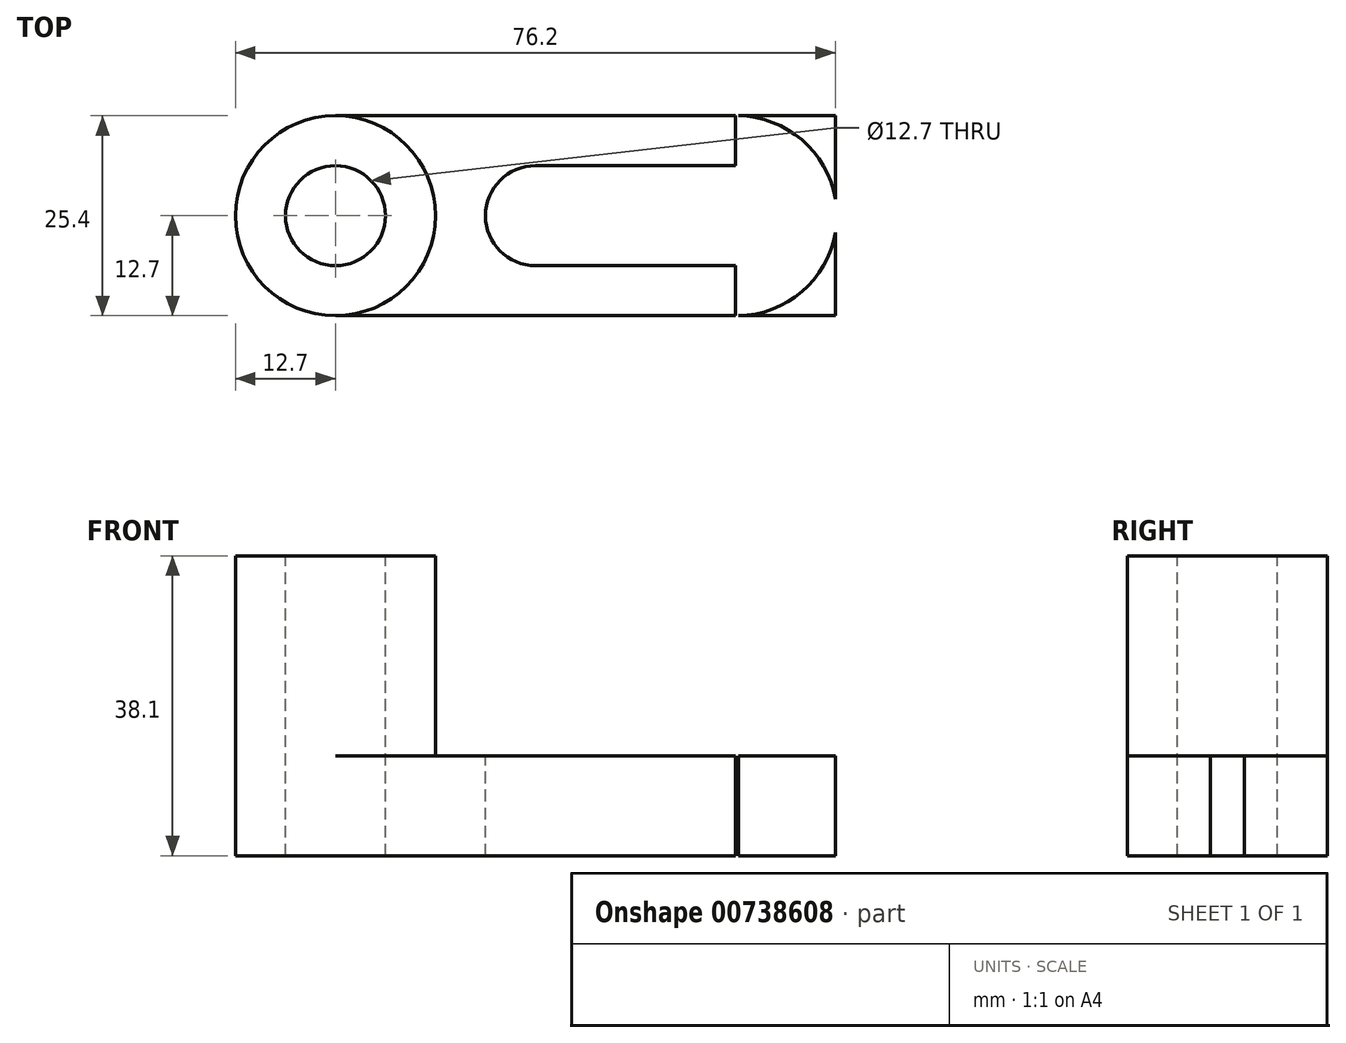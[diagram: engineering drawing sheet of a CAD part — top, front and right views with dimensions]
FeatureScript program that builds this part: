
annotation { "Feature Type Name" : "Feature", "Feature Type Description" : "" }
export const myFeature = defineFeature(function(context is Context, id is Id, definition is map)
    precondition{}
    {
        {
            var Q0;
            Q0=qCreatedBy(makeId("Front.planeOp"),FACE);
            var sketch = newSketch(context, id + "F0", { "sketchPlane" : qUnion([Q0])});
            skLineSegment(sketch, "E0", {"start": v(0, 38.1) * mm, "end": v(0, 0) * mm});
            skLineSegment(sketch, "E1", {"start": v(0, 0) * mm, "end": v(76.2, 0) * mm});
            skLineSegment(sketch, "E2", {"start": v(76.2, 0) * mm, "end": v(76.2, 12.7) * mm});
            skLineSegment(sketch, "E3", {"start": v(76.2, 12.7) * mm, "end": v(25.4, 12.7) * mm});
            skLineSegment(sketch, "E4", {"start": v(25.4, 12.7) * mm, "end": v(25.4, 38.1) * mm});
            skLineSegment(sketch, "E5", {"start": v(25.4, 38.1) * mm, "end": v(0, 38.1) * mm});
            skSolve(sketch);
        }
        {
            var Q0;
            Q0 = qSketchRegion(id + "F0", true);
            extrude(context, id + "F1", {"entities" : qUnion([Q0]), "depth" : 25.4 * mm, "offsetDistance" : 25.4 * mm});
        }
        {
            var Q0;
            Q0=makeQuery(id+"F1.opExtrude","SWEPT_FACE",FACE,{"disambiguationData":[OSD([sQuery(id+"F0.wireOp",EDGE,"E5")])]});
            var sketch = newSketch(context, id + "F2", { "sketchPlane" : qUnion([Q0])});
            skLineSegment(sketch, "E6", {"start": v(0, -12.7) * mm, "end": v(25.4, -12.7) * mm});
            skCircle(sketch, "E7", {"center": v(12.7, -12.7) * mm, "radius": 12.7 * mm});
            skCircle(sketch, "E8", {"center": v(12.7, -12.7) * mm, "radius": 6.35 * mm});
            skSolve(sketch);
        }
        {
            var Q0;
            {var subQ0=sQuery(id+"F2.wireOp",EDGE,"E8");var subQ1=sQuery(id+"F2.wireOp",EDGE,"E6");var subQ2=makeQuery(id+"F2.imprint","INTERSECT",VERTEX,{"disambiguationData":[OD(0.0)],"derivedFrom":[subQ1,subQ0]});Q0=makeQuery(id+"F2.imprint","IMPRINT",FACE,{"disambiguationData":[TD([[makeQuery(id+"F2.imprint","IMPRINT",EDGE,{"disambiguationData":[TD([[subQ2,-1.0]])],"derivedFrom":subQ1}),-1.0]])]});}
            var Q1;
            {var subQ0=sQuery(id+"F2.wireOp",EDGE,"E8");var subQ1=sQuery(id+"F2.wireOp",EDGE,"E6");var subQ2=makeQuery(id+"F2.imprint","INTERSECT",VERTEX,{"disambiguationData":[OD(0.0)],"derivedFrom":[subQ1,subQ0]});Q1=makeQuery(id+"F2.imprint","IMPRINT",FACE,{"disambiguationData":[TD([[makeQuery(id+"F2.imprint","IMPRINT",EDGE,{"disambiguationData":[TD([[subQ2,-1.0]])],"derivedFrom":subQ1}),1.0]])]});}
            var Q2;
            {var subQ0=sQuery(id+"F2.wireOp",EDGE,"E7");var subQ1=sQuery(id+"F0.wireOp",EDGE,"E5");var subQ4=makeQuery(id+"F1.opExtrude","CAP_EDGE",EDGE,{"disambiguationData":[OSD([subQ1])],"isStart":true});var subQ5=makeQuery(id+"F2.imprint","INTERSECT",VERTEX,{"derivedFrom":[subQ4,subQ0]});Q2=makeQuery(id+"F2.imprint","IMPRINT",FACE,{"disambiguationData":[TD([[makeQuery(id+"F2.imprint","IMPRINT",EDGE,{"disambiguationData":[TD([[subQ5,-1.0]])],"derivedFrom":subQ4}),1.0]])]});}
            var Q3;
            {var subQ0=sQuery(id+"F2.wireOp",EDGE,"E7");var subQ1=sQuery(id+"F0.wireOp",EDGE,"E5");var subQ4=makeQuery(id+"F1.opExtrude","CAP_EDGE",EDGE,{"disambiguationData":[OSD([subQ1])],"isStart":false});var subQ5=makeQuery(id+"F2.imprint","INTERSECT",VERTEX,{"derivedFrom":[subQ4,subQ0]});Q3=makeQuery(id+"F2.imprint","IMPRINT",FACE,{"disambiguationData":[TD([[makeQuery(id+"F2.imprint","IMPRINT",EDGE,{"disambiguationData":[TD([[subQ5,-1.0]])],"derivedFrom":subQ4}),-1.0]])]});}
            var Q4;
            {var subQ0=sQuery(id+"F2.wireOp",EDGE,"E7");var subQ1=sQuery(id+"F0.wireOp",EDGE,"E5");var subQ4=makeQuery(id+"F1.opExtrude","CAP_EDGE",EDGE,{"disambiguationData":[OSD([subQ1])],"isStart":true});var subQ5=makeQuery(id+"F2.imprint","INTERSECT",VERTEX,{"derivedFrom":[subQ4,subQ0]});Q4=makeQuery(id+"F2.imprint","IMPRINT",FACE,{"disambiguationData":[TD([[makeQuery(id+"F2.imprint","IMPRINT",EDGE,{"disambiguationData":[TD([[subQ5,1.0]])],"derivedFrom":subQ4}),1.0]])]});}
            var Q5;
            {var subQ0=sQuery(id+"F2.wireOp",EDGE,"E7");var subQ1=sQuery(id+"F0.wireOp",EDGE,"E5");var subQ4=makeQuery(id+"F1.opExtrude","CAP_EDGE",EDGE,{"disambiguationData":[OSD([subQ1])],"isStart":false});var subQ5=makeQuery(id+"F2.imprint","INTERSECT",VERTEX,{"derivedFrom":[subQ4,subQ0]});Q5=makeQuery(id+"F2.imprint","IMPRINT",FACE,{"disambiguationData":[TD([[makeQuery(id+"F2.imprint","IMPRINT",EDGE,{"disambiguationData":[TD([[subQ5,1.0]])],"derivedFrom":subQ4}),-1.0]])]});}
            extrude(context, id + "F3", {"entities" : qUnion([Q0, Q1, Q2, Q3, Q4, Q5]), "operationType" : NewBodyOperationType.REMOVE, "oppositeDirection" : true, "depth" : 25.4 * mm, "offsetDistance" : 25.4 * mm});
        }
        {
            var Q0;
            {var subQ0=sQuery(id+"F0.wireOp",EDGE,"E5");var subQ1=makeQuery(id+"F1.opExtrude","CAP_EDGE",EDGE,{"disambiguationData":[OSD([subQ0])],"isStart":true});var subQ2=sQuery(id+"F0.wireOp",EDGE,"E0");var subQ3=makeQuery(id+"F1.opExtrude","SWEPT_EDGE",EDGE,{"disambiguationData":[OSD([subQ2,subQ0])]});var subQ4=makeQuery(id+"F2.imprint","INTERSECT",VERTEX,{"derivedFrom":[subQ3,subQ1]});var subQ5=sQuery(id+"F2.wireOp",EDGE,"E7");var subQ6=makeQuery(id+"F2.imprint","INTERSECT",VERTEX,{"derivedFrom":[subQ1,subQ5]});Q0=makeQuery(id+"F3.boolean.opBoolean","COPY",FACE,{"derivedFrom":makeQuery(id+"F3.opExtrude","CAP_FACE",FACE,{"disambiguationData":[OSD([subQ2,subQ0,subQ5]),TDD([makeQuery(id+"F2.imprint","IMPRINT",EDGE,{"disambiguationData":[TD([[subQ6,-1.0]])],"derivedFrom":subQ5}),makeQuery(id+"F2.imprint","IMPRINT",EDGE,{"disambiguationData":[TD([[subQ4,1.0]])],"derivedFrom":subQ3}),makeQuery(id+"F2.imprint","IMPRINT",EDGE,{"disambiguationData":[TD([[subQ6,-1.0]])],"derivedFrom":subQ1})])],"isStart":false})});}
            var Q1;
            {var subQ0=sQuery(id+"F0.wireOp",EDGE,"E5");var subQ1=makeQuery(id+"F1.opExtrude","CAP_EDGE",EDGE,{"disambiguationData":[OSD([subQ0])],"isStart":false});var subQ2=sQuery(id+"F0.wireOp",EDGE,"E0");var subQ3=makeQuery(id+"F1.opExtrude","SWEPT_EDGE",EDGE,{"disambiguationData":[OSD([subQ2,subQ0])]});var subQ4=makeQuery(id+"F2.imprint","INTERSECT",VERTEX,{"derivedFrom":[subQ3,subQ1]});var subQ5=sQuery(id+"F2.wireOp",EDGE,"E7");var subQ6=makeQuery(id+"F2.imprint","INTERSECT",VERTEX,{"derivedFrom":[subQ1,subQ5]});Q1=makeQuery(id+"F3.boolean.opBoolean","COPY",FACE,{"derivedFrom":makeQuery(id+"F3.opExtrude","CAP_FACE",FACE,{"disambiguationData":[OSD([subQ2,subQ0,subQ5]),TDD([makeQuery(id+"F2.imprint","IMPRINT",EDGE,{"disambiguationData":[TD([[subQ6,1.0]])],"derivedFrom":subQ5}),makeQuery(id+"F2.imprint","IMPRINT",EDGE,{"disambiguationData":[TD([[subQ4,-1.0]])],"derivedFrom":subQ3}),makeQuery(id+"F2.imprint","IMPRINT",EDGE,{"disambiguationData":[TD([[subQ6,-1.0]])],"derivedFrom":subQ1})])],"isStart":false})});}
            extrude(context, id + "F4", {"entities" : qUnion([Q0, Q1]), "operationType" : NewBodyOperationType.REMOVE, "endBound" : BoundingType.THROUGH_ALL, "oppositeDirection" : true, "depth" : 25.4 * mm, "offsetDistance" : 25.4 * mm});
        }
        {
            var Q0;
            {var subQ0=sQuery(id+"F0.wireOp",EDGE,"E5");var subQ1=makeQuery(id+"F1.opExtrude","CAP_EDGE",EDGE,{"disambiguationData":[OSD([subQ0])],"isStart":false});var subQ2=sQuery(id+"F0.wireOp",EDGE,"E4");var subQ3=makeQuery(id+"F1.opExtrude","SWEPT_EDGE",EDGE,{"disambiguationData":[OSD([subQ2,subQ0])]});var subQ4=makeQuery(id+"F2.imprint","INTERSECT",VERTEX,{"derivedFrom":[subQ3,subQ1]});var subQ5=sQuery(id+"F2.wireOp",EDGE,"E7");var subQ6=makeQuery(id+"F2.imprint","INTERSECT",VERTEX,{"derivedFrom":[subQ1,subQ5]});var subQ8=makeQuery(id+"F1.opExtrude","CAP_EDGE",EDGE,{"disambiguationData":[OSD([subQ0])],"isStart":true});var subQ9=makeQuery(id+"F2.imprint","INTERSECT",VERTEX,{"derivedFrom":[subQ3,subQ8]});var subQ10=makeQuery(id+"F2.imprint","INTERSECT",VERTEX,{"derivedFrom":[subQ8,subQ5]});Q0=makeQuery(id+"F3.boolean.opBoolean","MERGE",FACE,{"derivedFrom":[makeQuery(id+"F1.opExtrude","SWEPT_FACE",FACE,{"disambiguationData":[OSD([sQuery(id+"F0.wireOp",EDGE,"E3")])]}),makeQuery(id+"F3.opExtrude","CAP_FACE",FACE,{"disambiguationData":[OSD([subQ2,subQ0,subQ5]),TDD([makeQuery(id+"F2.imprint","IMPRINT",EDGE,{"disambiguationData":[TD([[subQ10,1.0]])],"derivedFrom":subQ5}),makeQuery(id+"F2.imprint","IMPRINT",EDGE,{"disambiguationData":[TD([[subQ9,1.0]])],"derivedFrom":subQ3}),makeQuery(id+"F2.imprint","IMPRINT",EDGE,{"disambiguationData":[TD([[subQ10,1.0]])],"derivedFrom":subQ8})])],"isStart":false}),makeQuery(id+"F3.opExtrude","CAP_FACE",FACE,{"disambiguationData":[OSD([subQ2,subQ0,subQ5]),TDD([makeQuery(id+"F2.imprint","IMPRINT",EDGE,{"disambiguationData":[TD([[subQ6,-1.0]])],"derivedFrom":subQ5}),makeQuery(id+"F2.imprint","IMPRINT",EDGE,{"disambiguationData":[TD([[subQ4,-1.0]])],"derivedFrom":subQ3}),makeQuery(id+"F2.imprint","IMPRINT",EDGE,{"disambiguationData":[TD([[subQ6,1.0]])],"derivedFrom":subQ1})])],"isStart":false})]});}
            var sketch = newSketch(context, id + "F5", { "sketchPlane" : qUnion([Q0])});
            skLineSegment(sketch, "E9", {"start": v(63.5, 0) * mm, "end": v(63.5, -25.4) * mm});
            skLineSegment(sketch, "E10", {"start": v(38.1, 0) * mm, "end": v(38.1, -25.4) * mm});
            skCircle(sketch, "E11", {"center": v(38.1, -12.7) * mm, "radius": 6.35 * mm});
            skCircle(sketch, "E12", {"center": v(63.5, -12.7) * mm, "radius": 6.35 * mm});
            skLineSegment(sketch, "E13", {"start": v(38.1, -6.35) * mm, "end": v(63.5, -6.35) * mm});
            skLineSegment(sketch, "E14", {"start": v(38.1, -19.05) * mm, "end": v(63.5, -19.05) * mm});
            skArc(sketch, "E15", {"start": v(63.5, -25.4) * mm, "mid": v(76.38, -12.7) * mm, "end": v(63.5, 0) * mm});
            skSolve(sketch);
        }
        {
            var Q0;
            {var subQ0=sQuery(id+"F5.wireOp",EDGE,"E15");var subQ1=sQuery(id+"F0.wireOp",EDGE,"E5");var subQ2=makeQuery(id+"F1.opExtrude","CAP_EDGE",EDGE,{"disambiguationData":[OSD([subQ1])],"isStart":false});var subQ3=makeQuery(id+"F3.boolean.opBoolean","MERGE",EDGE,{"derivedFrom":[makeQuery(id+"F1.opExtrude","CAP_EDGE",EDGE,{"disambiguationData":[OSD([sQuery(id+"F0.wireOp",EDGE,"E3")])],"isStart":false}),makeQuery(id+"F3.opExtrude","CAP_EDGE",EDGE,{"disambiguationData":[OSD([subQ1]),TDD([makeQuery(id+"F2.imprint","IMPRINT",EDGE,{"disambiguationData":[TD([[makeQuery(id+"F2.imprint","INTERSECT",VERTEX,{"derivedFrom":[subQ2,sQuery(id+"F2.wireOp",EDGE,"E7")]}),1.0]])],"derivedFrom":subQ2})])],"isStart":false})]});var subQ5=makeQuery(id+"F5.imprint","INTERSECT",VERTEX,{"derivedFrom":[subQ3,subQ0]});Q0=makeQuery(id+"F5.imprint","IMPRINT",FACE,{"disambiguationData":[TD([[makeQuery(id+"F5.imprint","IMPRINT",EDGE,{"disambiguationData":[TD([[subQ5,1.0]])],"derivedFrom":subQ0}),1.0]])]});}
            var Q1;
            {var subQ0=sQuery(id+"F5.wireOp",EDGE,"E15");var subQ1=makeQuery(id+"F1.opExtrude","SWEPT_EDGE",EDGE,{"disambiguationData":[OSD([sQuery(id+"F0.wireOp",EDGE,"E2"),sQuery(id+"F0.wireOp",EDGE,"E3")])]});var subQ2=makeQuery(id+"F5.imprint","INTERSECT",VERTEX,{"disambiguationData":[OD(0.0)],"derivedFrom":[subQ1,subQ0]});Q1=makeQuery(id+"F5.imprint","IMPRINT",FACE,{"disambiguationData":[TD([[makeQuery(id+"F5.imprint","IMPRINT",EDGE,{"disambiguationData":[TD([[subQ2,-1.0]])],"derivedFrom":subQ0}),1.0]])]});}
            var Q2;
            {var subQ0=sQuery(id+"F5.wireOp",EDGE,"E15");var subQ1=sQuery(id+"F0.wireOp",EDGE,"E5");var subQ2=makeQuery(id+"F1.opExtrude","CAP_EDGE",EDGE,{"disambiguationData":[OSD([subQ1])],"isStart":true});var subQ3=makeQuery(id+"F3.boolean.opBoolean","MERGE",EDGE,{"derivedFrom":[makeQuery(id+"F1.opExtrude","CAP_EDGE",EDGE,{"disambiguationData":[OSD([sQuery(id+"F0.wireOp",EDGE,"E3")])],"isStart":true}),makeQuery(id+"F3.opExtrude","CAP_EDGE",EDGE,{"disambiguationData":[OSD([subQ1]),TDD([makeQuery(id+"F2.imprint","IMPRINT",EDGE,{"disambiguationData":[TD([[makeQuery(id+"F2.imprint","INTERSECT",VERTEX,{"derivedFrom":[subQ2,sQuery(id+"F2.wireOp",EDGE,"E7")]}),1.0]])],"derivedFrom":subQ2})])],"isStart":false})]});var subQ5=makeQuery(id+"F5.imprint","INTERSECT",VERTEX,{"derivedFrom":[subQ3,subQ0]});Q2=makeQuery(id+"F5.imprint","IMPRINT",FACE,{"disambiguationData":[TD([[makeQuery(id+"F5.imprint","IMPRINT",EDGE,{"disambiguationData":[TD([[subQ5,-1.0]])],"derivedFrom":subQ0}),1.0]])]});}
            var Q3;
            {var subQ0=sQuery(id+"F5.wireOp",EDGE,"E15");var subQ1=sQuery(id+"F0.wireOp",EDGE,"E3");var subQ2=makeQuery(id+"F1.opExtrude","SWEPT_EDGE",EDGE,{"disambiguationData":[OSD([sQuery(id+"F0.wireOp",EDGE,"E2"),subQ1])]});var subQ3=makeQuery(id+"F5.imprint","INTERSECT",VERTEX,{"disambiguationData":[OD(1.0)],"derivedFrom":[subQ2,subQ0]});Q3=makeQuery(id+"F5.imprint","IMPRINT",FACE,{"disambiguationData":[TD([[makeQuery(id+"F5.imprint","IMPRINT",EDGE,{"disambiguationData":[TD([[subQ3,-1.0]])],"derivedFrom":subQ0}),-1.0]])]});}
            var Q4;
            {var subQ0=sQuery(id+"F5.wireOp",EDGE,"E15");var subQ3=sQuery(id+"F0.wireOp",EDGE,"E3");var subQ6=makeQuery(id+"F1.opExtrude","SWEPT_EDGE",EDGE,{"disambiguationData":[OSD([sQuery(id+"F0.wireOp",EDGE,"E2"),subQ3])]});var subQ7=makeQuery(id+"F5.imprint","INTERSECT",VERTEX,{"disambiguationData":[OD(0.0)],"derivedFrom":[subQ6,subQ0]});Q4=makeQuery(id+"F5.imprint","IMPRINT",FACE,{"disambiguationData":[TD([[makeQuery(id+"F5.imprint","IMPRINT",EDGE,{"disambiguationData":[TD([[subQ7,1.0]])],"derivedFrom":subQ0}),-1.0]])]});}
            var Q5;
            {var subQ0=sQuery(id+"F5.wireOp",EDGE,"E12");var subQ1=sQuery(id+"F5.wireOp",EDGE,"E9");var subQ2=makeQuery(id+"F5.imprint","INTERSECT",VERTEX,{"derivedFrom":[subQ1,subQ0,sQuery(id+"F5.wireOp",EDGE,"E13")]});Q5=makeQuery(id+"F5.imprint","IMPRINT",FACE,{"disambiguationData":[TD([[makeQuery(id+"F5.imprint","IMPRINT",EDGE,{"disambiguationData":[TD([[subQ2,-1.0]])],"derivedFrom":subQ1}),1.0]])]});}
            var Q6;
            {var subQ0=sQuery(id+"F5.wireOp",EDGE,"E12");var subQ1=sQuery(id+"F5.wireOp",EDGE,"E9");var subQ2=makeQuery(id+"F5.imprint","INTERSECT",VERTEX,{"derivedFrom":[subQ1,subQ0,sQuery(id+"F5.wireOp",EDGE,"E13")]});Q6=makeQuery(id+"F5.imprint","IMPRINT",FACE,{"disambiguationData":[TD([[makeQuery(id+"F5.imprint","IMPRINT",EDGE,{"disambiguationData":[TD([[subQ2,-1.0]])],"derivedFrom":subQ1}),-1.0]])]});}
            var Q7;
            {var subQ0=sQuery(id+"F5.wireOp",EDGE,"E13");Q7=makeQuery(id+"F5.imprint","IMPRINT",FACE,{"disambiguationData":[TD([[makeQuery(id+"F5.imprint","IMPRINT",EDGE,{"derivedFrom":subQ0}),-1.0]])]});}
            var Q8;
            {var subQ0=sQuery(id+"F5.wireOp",EDGE,"E11");var subQ1=sQuery(id+"F5.wireOp",EDGE,"E10");var subQ2=makeQuery(id+"F5.imprint","INTERSECT",VERTEX,{"derivedFrom":[subQ1,subQ0,sQuery(id+"F5.wireOp",EDGE,"E13")]});Q8=makeQuery(id+"F5.imprint","IMPRINT",FACE,{"disambiguationData":[TD([[makeQuery(id+"F5.imprint","IMPRINT",EDGE,{"disambiguationData":[TD([[subQ2,-1.0]])],"derivedFrom":subQ1}),1.0]])]});}
            var Q9;
            {var subQ0=sQuery(id+"F5.wireOp",EDGE,"E11");var subQ1=sQuery(id+"F5.wireOp",EDGE,"E10");var subQ2=makeQuery(id+"F5.imprint","INTERSECT",VERTEX,{"derivedFrom":[subQ1,subQ0,sQuery(id+"F5.wireOp",EDGE,"E13")]});Q9=makeQuery(id+"F5.imprint","IMPRINT",FACE,{"disambiguationData":[TD([[makeQuery(id+"F5.imprint","IMPRINT",EDGE,{"disambiguationData":[TD([[subQ2,-1.0]])],"derivedFrom":subQ1}),-1.0]])]});}
            extrude(context, id + "F6", {"entities" : qUnion([Q0, Q1, Q2, Q3, Q4, Q5, Q6, Q7, Q8, Q9]), "operationType" : NewBodyOperationType.REMOVE, "endBound" : BoundingType.THROUGH_ALL, "oppositeDirection" : true, "depth" : 25.4 * mm, "offsetDistance" : 25.4 * mm});
        }
        {
            var Q0;
            Q0=makeQuery(id+"F3.boolean.opBoolean","COPY",FACE,{"derivedFrom":makeQuery(id+"F3.opExtrude","CAP_FACE",FACE,{"disambiguationData":[OSD([sQuery(id+"F2.wireOp",EDGE,"E8")])],"isStart":false})});
            extrude(context, id + "F7", {"entities" : qUnion([Q0]), "operationType" : NewBodyOperationType.REMOVE, "endBound" : BoundingType.THROUGH_ALL, "oppositeDirection" : true, "depth" : 25.4 * mm, "offsetDistance" : 25.4 * mm});
        }
    });
